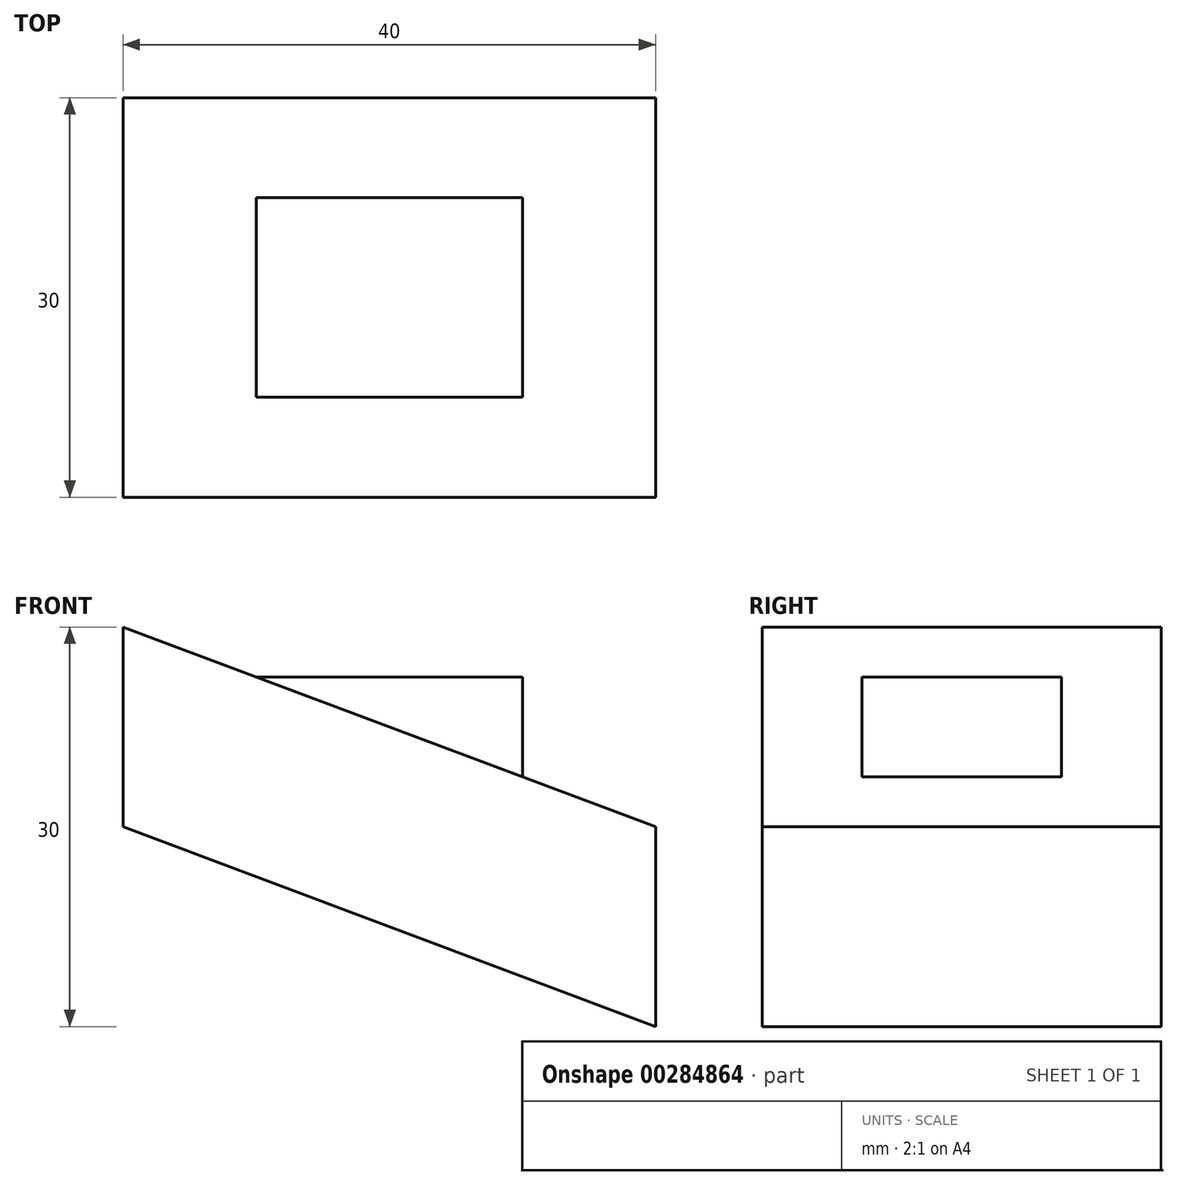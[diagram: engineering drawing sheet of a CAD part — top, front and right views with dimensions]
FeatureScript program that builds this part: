
annotation { "Feature Type Name" : "Feature", "Feature Type Description" : "" }
export const myFeature = defineFeature(function(context is Context, id is Id, definition is map)
    precondition{}
    {
        {
            var Q0;
            Q0=qCreatedBy(makeId("Front.planeOp"),FACE);
            var sketch = newSketch(context, id + "F0", { "sketchPlane" : qUnion([Q0])});
            skLineSegment(sketch, "E0.bottom", {"start": v(0, 0) * mm, "end": v(40, 0) * mm});
            skLineSegment(sketch, "E0.top", {"start": v(0, 30) * mm, "end": v(40, 30) * mm});
            skLineSegment(sketch, "E0.left", {"start": v(0, 0) * mm, "end": v(0, 30) * mm});
            skLineSegment(sketch, "E0.right", {"start": v(40, 0) * mm, "end": v(40, 30) * mm});
            skLineSegment(sketch, "E1", {"start": v(0, 30) * mm, "end": v(40, 15) * mm});
            skLineSegment(sketch, "E2.bottom", {"start": v(10, 26.25) * mm, "end": v(30, 26.25) * mm});
            skLineSegment(sketch, "E2.top", {"start": v(10, 18.75) * mm, "end": v(30, 18.75) * mm});
            skLineSegment(sketch, "E2.left", {"start": v(10, 26.25) * mm, "end": v(10, 18.75) * mm});
            skLineSegment(sketch, "E2.right", {"start": v(30, 26.25) * mm, "end": v(30, 18.75) * mm});
            skLineSegment(sketch, "E3", {"start": v(40, 0) * mm, "end": v(0, 15) * mm});
            skSolve(sketch);
        }
        {
            var Q0;
            {var subQ4=sQuery(id+"F0.wireOp",EDGE,"E0.bottom");Q0=makeQuery(id+"F0.imprint","IMPRINT",FACE,{"disambiguationData":[TD([[makeQuery(id+"F0.imprint","IMPRINT",EDGE,{"derivedFrom":subQ4}),1.0]])]});}
            var Q1;
            {var subQ2=sQuery(id+"F0.wireOp",EDGE,"E2.top");Q1=makeQuery(id+"F0.imprint","IMPRINT",FACE,{"disambiguationData":[TD([[makeQuery(id+"F0.imprint","IMPRINT",EDGE,{"derivedFrom":subQ2}),1.0]])]});}
            var Q2;
            {var subQ7=sQuery(id+"F0.wireOp",EDGE,"E2.top");Q2=makeQuery(id+"F0.imprint","IMPRINT",FACE,{"disambiguationData":[TD([[makeQuery(id+"F0.imprint","IMPRINT",EDGE,{"derivedFrom":subQ7}),-1.0]])]});}
            extrude(context, id + "F1", {"entities" : qUnion([Q0, Q1, Q2]), "depth" : 30 * mm, "symmetric" : true});
        }
        {
            var Q0;
            {var subQ0=sQuery(id+"F0.wireOp",EDGE,"E2.bottom");Q0=makeQuery(id+"F0.imprint","IMPRINT",FACE,{"disambiguationData":[TD([[makeQuery(id+"F0.imprint","IMPRINT",EDGE,{"derivedFrom":subQ0}),-1.0]])]});}
            extrude(context, id + "F2", {"entities" : qUnion([Q0]), "operationType" : NewBodyOperationType.ADD, "oppositeDirection" : true, "depth" : 15 * mm, "symmetric" : true});
        }
        {
            var Q0;
            {var subQ0=sQuery(id+"F0.wireOp",EDGE,"E0.bottom");Q0=makeQuery(id+"F0.imprint","IMPRINT",FACE,{"disambiguationData":[TD([[makeQuery(id+"F0.imprint","IMPRINT",EDGE,{"derivedFrom":subQ0}),1.0]])]});}
            extrude(context, id + "F3", {"entities" : qUnion([Q0]), "operationType" : NewBodyOperationType.REMOVE, "oppositeDirection" : true, "depth" : 30 * mm, "symmetric" : true});
        }
    });
